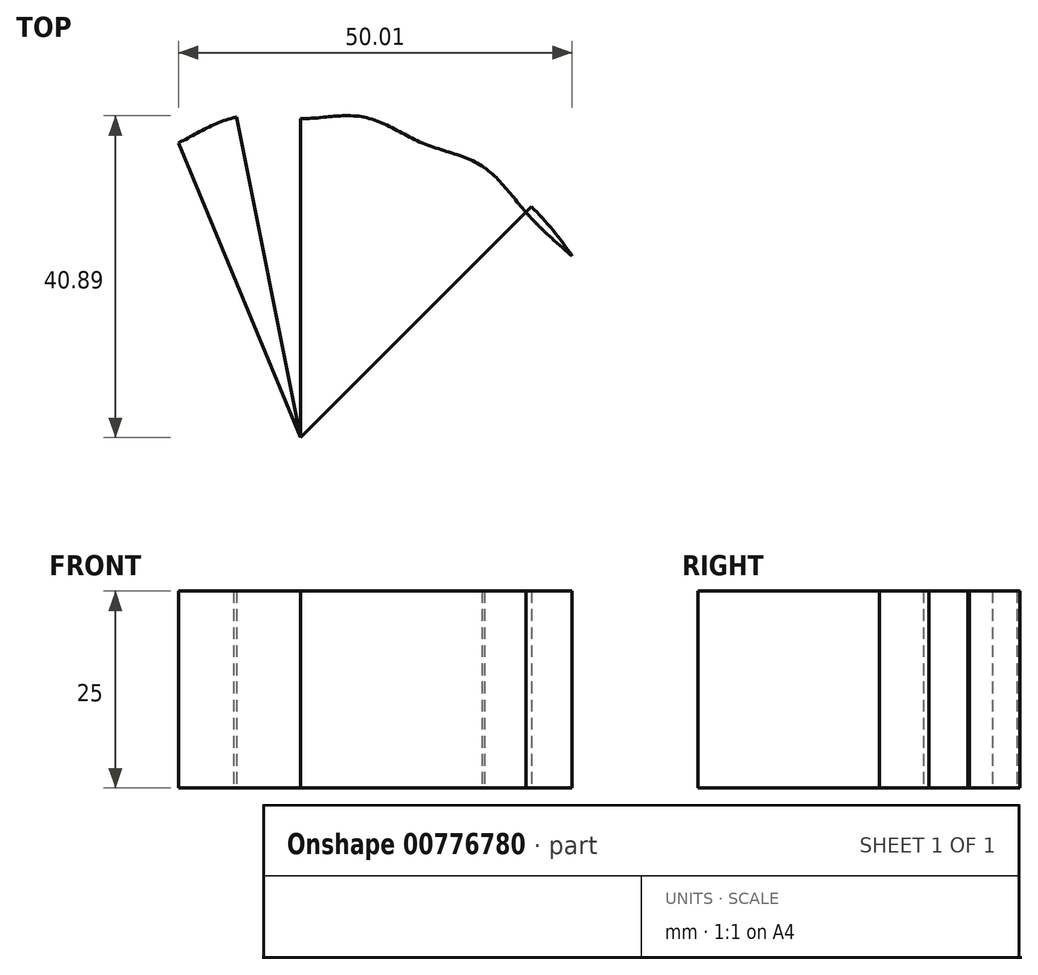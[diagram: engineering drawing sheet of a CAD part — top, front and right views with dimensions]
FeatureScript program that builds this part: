
annotation { "Feature Type Name" : "Feature", "Feature Type Description" : "" }
export const myFeature = defineFeature(function(context is Context, id is Id, definition is map)
    precondition{}
    {
        {
            var Q0;
            Q0=qCreatedBy(makeId("Top.planeOp"),FACE);
            var sketch = newSketch(context, id + "F0", { "sketchPlane" : qUnion([Q0])});
            skCircle(sketch, "E0", {"center": v(0, 0) * mm, "radius": 41.5 * mm});
            skLineSegment(sketch, "E1", {"start": v(0, 0) * mm, "end": v(0, 41.5) * mm});
            skLineSegment(sketch, "E2.1.0", {"start": v(0, 0) * mm, "end": v(-8.1, 40.7) * mm});
            skLineSegment(sketch, "E2.2.0", {"start": v(0, 0) * mm, "end": v(-15.88, 38.34) * mm});
            skLineSegment(sketch, "E2.3.0", {"start": v(0, 0) * mm, "end": v(-23.06, 34.5) * mm});
            skLineSegment(sketch, "E2.4.0", {"start": v(0, 0) * mm, "end": v(-29.34, 29.34) * mm});
            skLineSegment(sketch, "E2.5.0", {"start": v(0, 0) * mm, "end": v(-34.5, 23.06) * mm});
            skLineSegment(sketch, "E2.6.0", {"start": v(0, 0) * mm, "end": v(-38.34, 15.88) * mm});
            skLineSegment(sketch, "E2.7.0", {"start": v(0, 0) * mm, "end": v(-40.7, 8.1) * mm});
            skLineSegment(sketch, "E2.8.0", {"start": v(0, 0) * mm, "end": v(-41.5, 0) * mm});
            skLineSegment(sketch, "E2.9.0", {"start": v(0, 0) * mm, "end": v(-40.7, -8.1) * mm});
            skLineSegment(sketch, "E2.10.0", {"start": v(0, 0) * mm, "end": v(-38.34, -15.88) * mm});
            skLineSegment(sketch, "E2.11.0", {"start": v(0, 0) * mm, "end": v(-34.5, -23.06) * mm});
            skLineSegment(sketch, "E2.12.0", {"start": v(0, 0) * mm, "end": v(-29.34, -29.34) * mm});
            skLineSegment(sketch, "E2.13.0", {"start": v(0, 0) * mm, "end": v(-23.06, -34.5) * mm});
            skLineSegment(sketch, "E2.14.0", {"start": v(0, 0) * mm, "end": v(-15.88, -38.34) * mm});
            skLineSegment(sketch, "E2.15.0", {"start": v(0, 0) * mm, "end": v(-8.1, -40.7) * mm});
            skCircle(sketch, "E3", {"center": v(0, 0) * mm, "radius": 40.5 * mm});
            skLineSegment(sketch, "E4.2.16.0", {"start": v(0, 0) * mm, "end": v(0, -41.5) * mm});
            skLineSegment(sketch, "E4.2.17.0", {"start": v(0, 0) * mm, "end": v(8.1, -40.7) * mm});
            skLineSegment(sketch, "E4.2.18.0", {"start": v(0, 0) * mm, "end": v(15.88, -38.34) * mm});
            skLineSegment(sketch, "E4.2.19.0", {"start": v(0, 0) * mm, "end": v(23.06, -34.5) * mm});
            skLineSegment(sketch, "E4.2.20.0", {"start": v(0, 0) * mm, "end": v(29.34, -29.34) * mm});
            skLineSegment(sketch, "E4.2.21.0", {"start": v(0, 0) * mm, "end": v(34.5, -23.06) * mm});
            skLineSegment(sketch, "E4.2.22.0", {"start": v(0, 0) * mm, "end": v(38.34, -15.88) * mm});
            skLineSegment(sketch, "E4.2.23.0", {"start": v(0, 0) * mm, "end": v(40.7, -8.1) * mm});
            skLineSegment(sketch, "E4.2.24.0", {"start": v(0, 0) * mm, "end": v(41.5, 0) * mm});
            skLineSegment(sketch, "E4.2.25.0", {"start": v(0, 0) * mm, "end": v(40.7, 8.1) * mm});
            skLineSegment(sketch, "E4.2.26.0", {"start": v(0, 0) * mm, "end": v(38.34, 15.88) * mm});
            skLineSegment(sketch, "E4.2.27.0", {"start": v(0, 0) * mm, "end": v(34.5, 23.06) * mm});
            skLineSegment(sketch, "E4.2.28.0", {"start": v(0, 0) * mm, "end": v(29.34, 29.34) * mm});
            skLineSegment(sketch, "E4.2.29.0", {"start": v(0, 0) * mm, "end": v(23.06, 34.5) * mm});
            skLineSegment(sketch, "E4.2.30.0", {"start": v(0, 0) * mm, "end": v(15.88, 38.34) * mm});
            skLineSegment(sketch, "E4.2.31.0", {"start": v(0, 0) * mm, "end": v(8.1, 40.7) * mm});
            skFitSpline(sketch, "E5", {"points": [v(-23.06, 34.5) * mm, v(-15.5, 37.42) * mm, v(-8.1, 40.7) * mm, v(0, 40.5) * mm, v(8.1, 40.7) * mm, v(15.5, 37.42) * mm, v(23.06, 34.5) * mm, v(28.64, 28.64) * mm, v(34.5, 23.06) * mm], "startDerivative": vector(61.15, 20.26) * mm, "endDerivative": vector(48.74, -42.12) * mm});
            skSolve(sketch);
        }
        {
            var Q0;
            {var subQ1=sQuery(id+"F0.wireOp",EDGE,"E2.1.0");var subQ3=sQuery(id+"F0.wireOp",EDGE,"E3");var subQ4=makeQuery(id+"F0.imprint","INTERSECT",VERTEX,{"derivedFrom":[subQ1,subQ3]});Q0=makeQuery(id+"F0.imprint","IMPRINT",FACE,{"disambiguationData":[TD([[makeQuery(id+"F0.imprint","IMPRINT",EDGE,{"disambiguationData":[TD([[subQ4,-1.0]])],"derivedFrom":subQ3}),1.0]])]});}
            var Q1;
            {var subQ0=sQuery(id+"F0.wireOp",EDGE,"E5");var subQ2=sQuery(id+"F0.wireOp",EDGE,"E0");var subQ4=makeQuery(id+"F0.imprint","INTERSECT",VERTEX,{"disambiguationData":[OD(1.0)],"derivedFrom":[subQ2,subQ0]});Q1=makeQuery(id+"F0.imprint","IMPRINT",FACE,{"disambiguationData":[TD([[makeQuery(id+"F0.imprint","IMPRINT",EDGE,{"disambiguationData":[TD([[subQ4,1.0]])],"derivedFrom":subQ2}),1.0]])]});}
            var Q2;
            {var subQ0=sQuery(id+"F0.wireOp",EDGE,"E5");var subQ3=sQuery(id+"F0.wireOp",EDGE,"E3");var subQ5=makeQuery(id+"F0.imprint","INTERSECT",VERTEX,{"disambiguationData":[OD(0.0)],"derivedFrom":[subQ3,subQ0]});Q2=makeQuery(id+"F0.imprint","IMPRINT",FACE,{"disambiguationData":[TD([[makeQuery(id+"F0.imprint","IMPRINT",EDGE,{"disambiguationData":[TD([[subQ5,-1.0]])],"derivedFrom":subQ3}),-1.0]])]});}
            var Q3;
            {var subQ0=sQuery(id+"F0.wireOp",EDGE,"E4.2.31.0");var subQ1=sQuery(id+"F0.wireOp",EDGE,"E3");var subQ2=makeQuery(id+"F0.imprint","INTERSECT",VERTEX,{"derivedFrom":[subQ1,subQ0]});Q3=makeQuery(id+"F0.imprint","IMPRINT",FACE,{"disambiguationData":[TD([[makeQuery(id+"F0.imprint","IMPRINT",EDGE,{"disambiguationData":[TD([[subQ2,-1.0]])],"derivedFrom":subQ1}),-1.0]])]});}
            var Q4;
            {var subQ0=sQuery(id+"F0.wireOp",EDGE,"E4.2.31.0");var subQ1=sQuery(id+"F0.wireOp",EDGE,"E3");var subQ2=makeQuery(id+"F0.imprint","INTERSECT",VERTEX,{"derivedFrom":[subQ1,subQ0]});Q4=makeQuery(id+"F0.imprint","IMPRINT",FACE,{"disambiguationData":[TD([[makeQuery(id+"F0.imprint","IMPRINT",EDGE,{"disambiguationData":[TD([[subQ2,1.0]])],"derivedFrom":subQ1}),-1.0]])]});}
            var Q5;
            {var subQ0=sQuery(id+"F0.wireOp",EDGE,"E4.2.29.0");var subQ1=sQuery(id+"F0.wireOp",EDGE,"E3");var subQ2=makeQuery(id+"F0.imprint","INTERSECT",VERTEX,{"derivedFrom":[subQ1,subQ0]});Q5=makeQuery(id+"F0.imprint","IMPRINT",FACE,{"disambiguationData":[TD([[makeQuery(id+"F0.imprint","IMPRINT",EDGE,{"disambiguationData":[TD([[subQ2,-1.0]])],"derivedFrom":subQ1}),-1.0]])]});}
            var Q6;
            {var subQ0=sQuery(id+"F0.wireOp",EDGE,"E5");var subQ2=sQuery(id+"F0.wireOp",EDGE,"E0");var subQ4=makeQuery(id+"F0.imprint","INTERSECT",VERTEX,{"disambiguationData":[OD(0.0)],"derivedFrom":[subQ2,subQ0]});Q6=makeQuery(id+"F0.imprint","IMPRINT",FACE,{"disambiguationData":[TD([[makeQuery(id+"F0.imprint","IMPRINT",EDGE,{"disambiguationData":[TD([[subQ4,-1.0]])],"derivedFrom":subQ2}),1.0]])]});}
            var Q7;
            {var subQ0=sQuery(id+"F0.wireOp",EDGE,"E4.2.29.0");var subQ1=sQuery(id+"F0.wireOp",EDGE,"E3");var subQ2=makeQuery(id+"F0.imprint","INTERSECT",VERTEX,{"derivedFrom":[subQ1,subQ0]});Q7=makeQuery(id+"F0.imprint","IMPRINT",FACE,{"disambiguationData":[TD([[makeQuery(id+"F0.imprint","IMPRINT",EDGE,{"disambiguationData":[TD([[subQ2,1.0]])],"derivedFrom":subQ1}),1.0]])]});}
            var Q8;
            {var subQ0=sQuery(id+"F0.wireOp",EDGE,"E4.2.29.0");var subQ1=sQuery(id+"F0.wireOp",EDGE,"E3");var subQ2=makeQuery(id+"F0.imprint","INTERSECT",VERTEX,{"derivedFrom":[subQ1,subQ0]});Q8=makeQuery(id+"F0.imprint","IMPRINT",FACE,{"disambiguationData":[TD([[makeQuery(id+"F0.imprint","IMPRINT",EDGE,{"disambiguationData":[TD([[subQ2,-1.0]])],"derivedFrom":subQ1}),1.0]])]});}
            var Q9;
            {var subQ0=sQuery(id+"F0.wireOp",EDGE,"E4.2.31.0");var subQ1=sQuery(id+"F0.wireOp",EDGE,"E3");var subQ2=makeQuery(id+"F0.imprint","INTERSECT",VERTEX,{"derivedFrom":[subQ1,subQ0]});Q9=makeQuery(id+"F0.imprint","IMPRINT",FACE,{"disambiguationData":[TD([[makeQuery(id+"F0.imprint","IMPRINT",EDGE,{"disambiguationData":[TD([[subQ2,1.0]])],"derivedFrom":subQ1}),1.0]])]});}
            var Q10;
            {var subQ0=sQuery(id+"F0.wireOp",EDGE,"E4.2.31.0");var subQ3=sQuery(id+"F0.wireOp",EDGE,"E3");var subQ5=makeQuery(id+"F0.imprint","INTERSECT",VERTEX,{"derivedFrom":[subQ3,subQ0]});Q10=makeQuery(id+"F0.imprint","IMPRINT",FACE,{"disambiguationData":[TD([[makeQuery(id+"F0.imprint","IMPRINT",EDGE,{"disambiguationData":[TD([[subQ5,-1.0]])],"derivedFrom":subQ3}),1.0]])]});}
            var Q11;
            {var subQ3=sQuery(id+"F0.wireOp",EDGE,"E5");var subQ4=sQuery(id+"F0.wireOp",EDGE,"E3");var subQ7=makeQuery(id+"F0.imprint","INTERSECT",VERTEX,{"disambiguationData":[OD(0.0)],"derivedFrom":[subQ4,subQ3]});Q11=makeQuery(id+"F0.imprint","IMPRINT",FACE,{"disambiguationData":[TD([[makeQuery(id+"F0.imprint","IMPRINT",EDGE,{"disambiguationData":[TD([[subQ7,-1.0]])],"derivedFrom":subQ4}),1.0]])]});}
            extrude(context, id + "F1", {"entities" : qUnion([Q0, Q1, Q2, Q3, Q4, Q5, Q6, Q7, Q8, Q9, Q10, Q11]), "depth" : 25 * mm, "offsetDistance" : 25 * mm});
        }
    });
